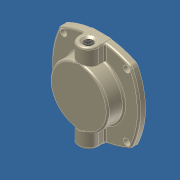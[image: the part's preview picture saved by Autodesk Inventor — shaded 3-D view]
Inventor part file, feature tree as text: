
AUTODESK INVENTOR PART (.ipt)
format: ipt  version: unknown  size: 513,024 bytes
history: native  units: in
note: dims shown in document units (in); Inventor stores cm internally (conversion verified against a paired STEP export)
features: extrude x8, sketch x8, plane x4, loft x2, thread x2, fillet x2, projected_geometry x1
ambient origin geometry x8: Origin, YZ Plane, XZ Plane, XY Plane, X Axis, Y Axis, Z Axis, Center Point
bodies: Solid1 (feature_tree)
feature tree (27):
  extrude  "Extrusion1"  Depth=0.25in
  extrude  "Extrusion2"  Depth=2.425in
  plane  "Work Plane1"
  sketch  "Sketch3"  dims[d7=0.25in d8=0.0in d9=2.225in]
  plane  "Work Plane2"
  extrude  "Extrusion3"  Depth=2.225in
  sketch  "Sketch4"  dims[d10=0.625in d11=0.0in d12=0.75in]
  plane  "Work Plane3"
  loft  "Loft1"
  extrude  "Extrusion5"  Depth=0.5in
  extrude  "Extrusion6"  Depth=2.125in
  sketch  "Sketch6"  dims[d15=0.625in d16=0.0in d19=2.125in]
  extrude  "Extrusion7"  Depth=2.0in
  extrude  "Extrusion8"  TaperAngle=0.0deg  [1 undecoded]
  plane  "Work Plane4"
  loft  "Loft2"
  thread  "Thread1"  [1 undecoded]
  thread  "Thread2"  [1 undecoded]
  fillet  "Fillet1"  Radius=0.05in
  extrude  "Extrusion9"  Depth=0.35in
  fillet  "Fillet2"  Radius=0.05in
  sketch  "Sketch1"  dims[d1=3.375in d2=0.25in]
  sketch  "Sketch2"  dims[d3=2.425in d4=2.425in]
  sketch  "Sketch5"  dims[d13=-3.375in d14=0.5in]
  sketch  "Sketch7"  dims[d20=-0.75in d21=2.0in]
  projected_geometry  "Projected Loop1"
  sketch  "Sketch8"  dims[d22=0.0in d23=90.0deg d24=0.0in d25=90.0deg d26=2.5in d27=2.625in d28=0.05in d29=0.0in d30=0.05in d31=0.0in d32=0.35in d33=0.05in d34=0.0in d35=0.55in d36=0.0125in d37=0.0in d38=-0.075in d39=0.0in d40=90.0deg d41=0.0in d42=90.0deg d43=0.39in d44=0.0in d45=1.0in d46=0.0in d48=0.0625in d49=0.625in d50=0.125in d51=0.0in d52=0.0375in d53=0.25in d54=2.425in d55=2.425in d56=3.375in d57=0.1in d58=0.1in d59=0.1in d60=0.1in d61=2.6693in d62=2.6693in]
note: 3 required parameter values undecoded (feature->parameter linkage not recoverable at this tier; creation-order binding heuristic only, values carry confidence <= 0.55)
